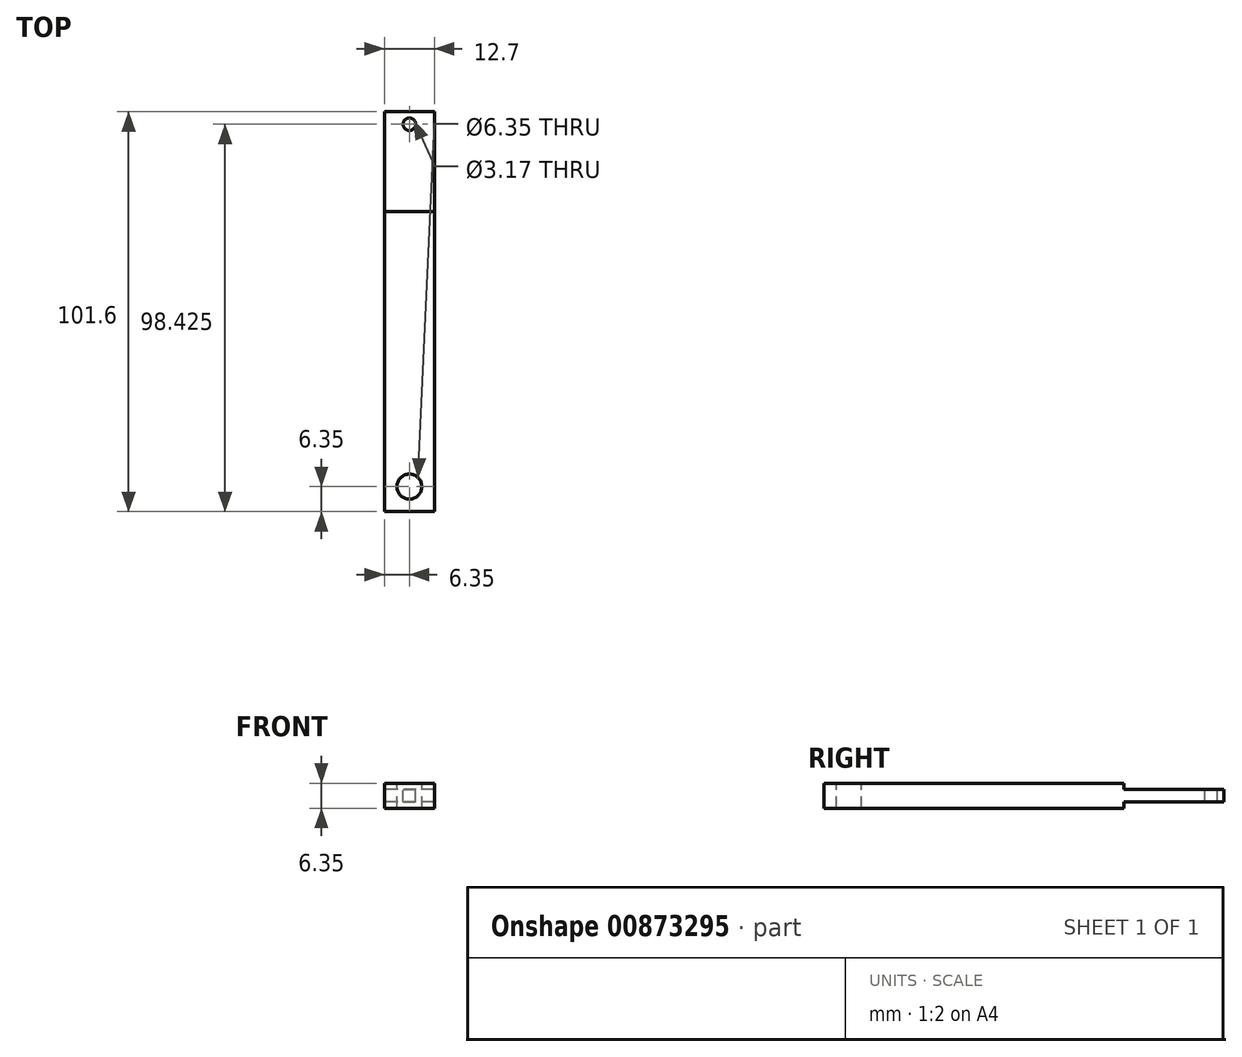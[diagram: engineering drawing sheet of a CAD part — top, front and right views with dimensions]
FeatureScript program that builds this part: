
annotation { "Feature Type Name" : "Feature", "Feature Type Description" : "" }
export const myFeature = defineFeature(function(context is Context, id is Id, definition is map)
    precondition{}
    {
        {
            var Q0;
            Q0=qCreatedBy(makeId("Front.planeOp"),FACE);
            var sketch = newSketch(context, id + "F0", { "sketchPlane" : qUnion([Q0])});
            skLineSegment(sketch, "E0.bottom", {"start": v(0, 0) * mm, "end": v(12.7, 0) * mm});
            skLineSegment(sketch, "E0.top", {"start": v(0, 6.35) * mm, "end": v(12.7, 6.35) * mm});
            skLineSegment(sketch, "E0.left", {"start": v(0, 0) * mm, "end": v(0, 6.35) * mm});
            skLineSegment(sketch, "E0.right", {"start": v(12.7, 0) * mm, "end": v(12.7, 6.35) * mm});
            skSolve(sketch);
        }
        {
            var Q0;
            Q0=makeQuery(id+"F0.imprint","IMPRINT",FACE,{"disambiguationData":[TD([[makeQuery(id+"F0.imprint","IMPRINT",EDGE,{"derivedFrom":sQuery(id+"F0.wireOp",EDGE,"E0.bottom")}),1.0]])]});
            extrude(context, id + "F1", {"entities" : qUnion([Q0]), "oppositeDirection" : true, "depth" : 101.6 * mm, "offsetDistance" : 25.4 * mm});
        }
        {
            var Q0;
            Q0=makeQuery(id+"F1.opExtrude","SWEPT_FACE",FACE,{"disambiguationData":[OSD([sQuery(id+"F0.wireOp",EDGE,"E0.top")])]});
            var sketch = newSketch(context, id + "F2", { "sketchPlane" : qUnion([Q0])});
            skCircle(sketch, "E1", {"center": v(6.35, 6.35) * mm, "radius": 3.18 * mm});
            skPoint(sketch, "E1.centerSnap0", {"position": v(6.35, 0) * mm});
            skCircle(sketch, "E2", {"center": v(6.35, 98.43) * mm, "radius": 1.59 * mm});
            skSolve(sketch);
        }
        {
            var Q0;
            Q0=makeQuery(id+"F2.imprint","IMPRINT",FACE,{"disambiguationData":[TD([[makeQuery(id+"F2.imprint","IMPRINT",EDGE,{"derivedFrom":sQuery(id+"F2.wireOp",EDGE,"E2")}),1.0]])]});
            var Q1;
            Q1=makeQuery(id+"F2.imprint","IMPRINT",FACE,{"disambiguationData":[TD([[makeQuery(id+"F2.imprint","IMPRINT",EDGE,{"derivedFrom":sQuery(id+"F2.wireOp",EDGE,"E1")}),1.0]])]});
            extrude(context, id + "F3", {"entities" : qUnion([Q0, Q1]), "operationType" : NewBodyOperationType.REMOVE, "endBound" : BoundingType.THROUGH_ALL, "oppositeDirection" : true, "depth" : 25.4 * mm, "offsetDistance" : 25.4 * mm});
        }
        {
            var Q0;
            Q0=makeQuery(id+"F1.opExtrude","CAP_FACE",FACE,{"disambiguationData":[OSD([sQuery(id+"F0.wireOp",EDGE,"E0.bottom"),sQuery(id+"F0.wireOp",EDGE,"E0.top"),sQuery(id+"F0.wireOp",EDGE,"E0.left"),sQuery(id+"F0.wireOp",EDGE,"E0.right")])],"isStart":false});
            var sketch = newSketch(context, id + "F4", { "sketchPlane" : qUnion([Q0])});
            skLineSegment(sketch, "E3", {"start": v(-16.56, 4.76) * mm, "end": v(2.9, 4.76) * mm});
            skLineSegment(sketch, "E4", {"start": v(-16.56, 1.59) * mm, "end": v(2.9, 1.59) * mm});
            skSolve(sketch);
        }
        {
            var Q0;
            {var subQ5=makeQuery(id+"F1.opExtrude","CAP_EDGE",EDGE,{"disambiguationData":[OSD([sQuery(id+"F0.wireOp",EDGE,"E0.top")])],"isStart":false});Q0=makeQuery(id+"F4.imprint","IMPRINT",FACE,{"disambiguationData":[TD([[makeQuery(id+"F4.imprint","IMPRINT",EDGE,{"derivedFrom":subQ5}),1.0]])]});}
            var Q1;
            {var subQ5=makeQuery(id+"F1.opExtrude","CAP_EDGE",EDGE,{"disambiguationData":[OSD([sQuery(id+"F0.wireOp",EDGE,"E0.bottom")])],"isStart":false});Q1=makeQuery(id+"F4.imprint","IMPRINT",FACE,{"disambiguationData":[TD([[makeQuery(id+"F4.imprint","IMPRINT",EDGE,{"derivedFrom":subQ5}),-1.0]])]});}
            extrude(context, id + "F5", {"entities" : qUnion([Q0, Q1]), "operationType" : NewBodyOperationType.REMOVE, "oppositeDirection" : true, "depth" : 25.4 * mm, "offsetDistance" : 25.4 * mm});
        }
    });
